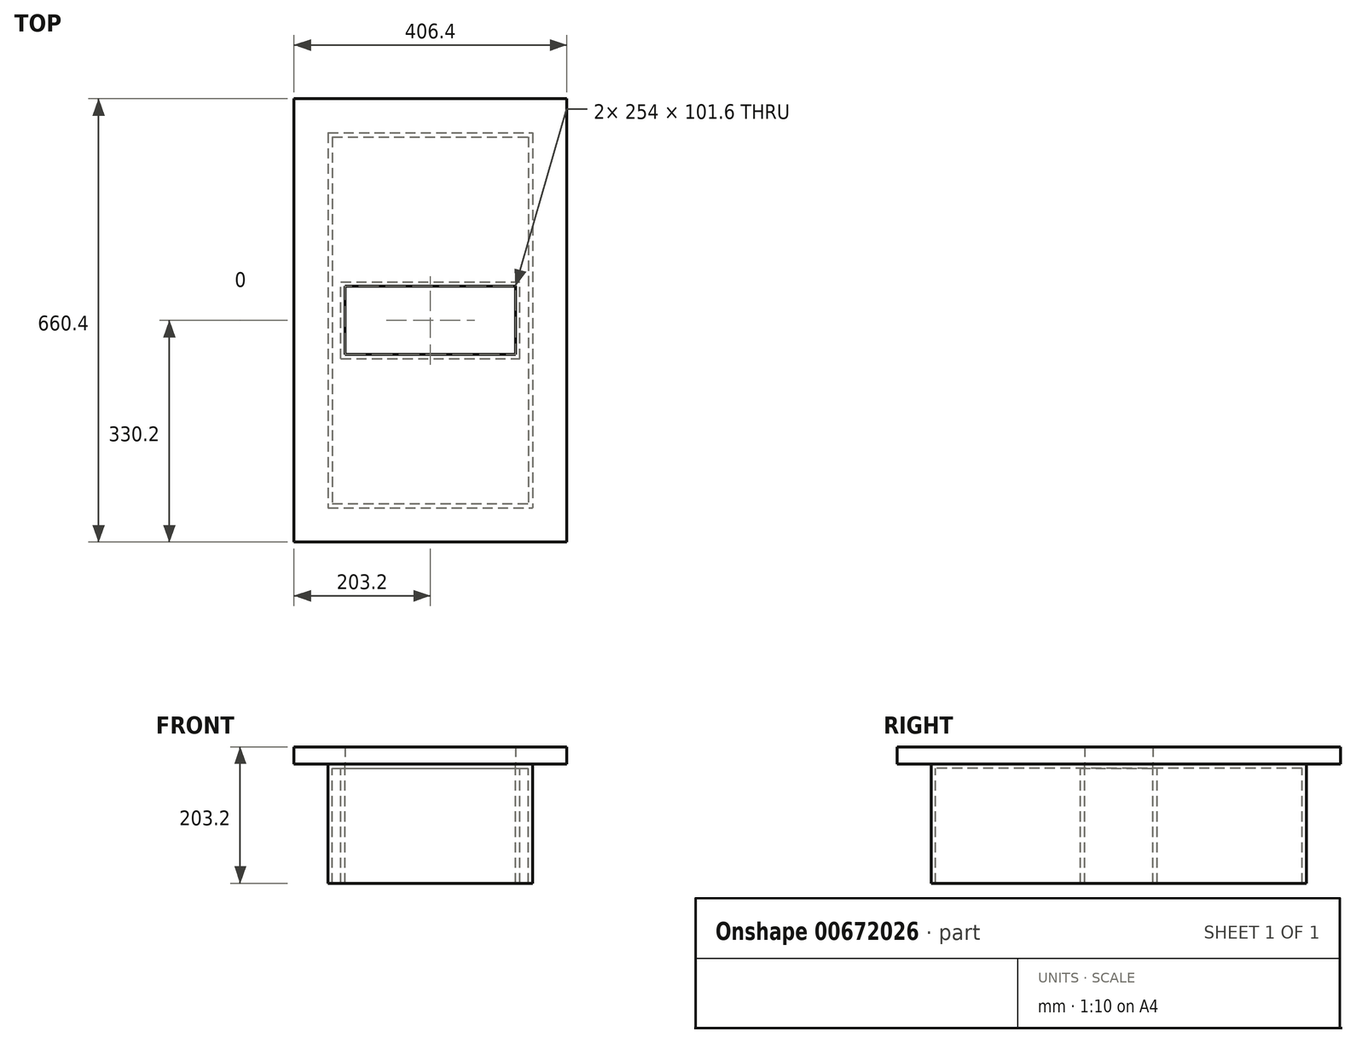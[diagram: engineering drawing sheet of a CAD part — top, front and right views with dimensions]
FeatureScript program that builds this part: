
annotation { "Feature Type Name" : "Feature", "Feature Type Description" : "" }
export const myFeature = defineFeature(function(context is Context, id is Id, definition is map)
    precondition{}
    {
        {
            var Q0;
            Q0=qCreatedBy(makeId("Top.planeOp"),FACE);
            var sketch = newSketch(context, id + "F0", { "sketchPlane" : qUnion([Q0])});
            skLineSegment(sketch, "E0.bottom", {"start": v(152.4, 381) * mm, "end": v(-254, 381) * mm});
            skLineSegment(sketch, "E0.top", {"start": v(152.4, -279.4) * mm, "end": v(-254, -279.4) * mm});
            skLineSegment(sketch, "E0.left", {"start": v(152.4, 381) * mm, "end": v(152.4, -279.4) * mm});
            skLineSegment(sketch, "E0.right", {"start": v(-254, 381) * mm, "end": v(-254, -279.4) * mm});
            skPoint(sketch, "E1", {"position": v(-203.2, 330.2) * mm});
            skPoint(sketch, "E2", {"position": v(101.6, -228.6) * mm});
            skLineSegment(sketch, "E3.bottom", {"start": v(-203.2, 330.2) * mm, "end": v(101.6, 330.2) * mm});
            skLineSegment(sketch, "E3.top", {"start": v(-203.2, -228.6) * mm, "end": v(101.6, -228.6) * mm});
            skLineSegment(sketch, "E3.left", {"start": v(-203.2, 330.2) * mm, "end": v(-203.2, -228.6) * mm});
            skLineSegment(sketch, "E3.right", {"start": v(101.6, 330.2) * mm, "end": v(101.6, -228.6) * mm});
            skLineSegment(sketch, "E4", {"start": v(-177.8, 50.8) * mm, "end": v(76.2, 50.8) * mm, "construction": true});
            skPoint(sketch, "E5", {"position": v(-50.8, 50.8) * mm});
            skPoint(sketch, "E5.positionSnap0", {"position": v(-50.8, 330.2) * mm});
            skLineSegment(sketch, "E6.bottom", {"start": v(-177.8, 0) * mm, "end": v(76.2, 0) * mm});
            skLineSegment(sketch, "E6.top", {"start": v(-177.8, 101.6) * mm, "end": v(76.2, 101.6) * mm});
            skLineSegment(sketch, "E6.left", {"start": v(-177.8, 0) * mm, "end": v(-177.8, 101.6) * mm});
            skLineSegment(sketch, "E6.right", {"start": v(76.2, 0) * mm, "end": v(76.2, 101.6) * mm});
            skSolve(sketch);
        }
        {
            var Q0;
            Q0=makeQuery(id+"F0.imprint","IMPRINT",FACE,{"disambiguationData":[TD([[makeQuery(id+"F0.imprint","IMPRINT",EDGE,{"derivedFrom":sQuery(id+"F0.wireOp",EDGE,"E0.bottom")}),1.0]])]});
            var sketch = newSketch(context, id + "F1", { "sketchPlane" : qUnion([Q0])});
            skSolve(sketch);
        }
        {
            var Q0;
            Q0=makeQuery(id+"F0.imprint","IMPRINT",FACE,{"disambiguationData":[TD([[makeQuery(id+"F0.imprint","IMPRINT",EDGE,{"derivedFrom":sQuery(id+"F0.wireOp",EDGE,"E3.bottom")}),-1.0]])]});
            var Q1;
            Q1=makeQuery(id+"F0.imprint","IMPRINT",FACE,{"disambiguationData":[TD([[makeQuery(id+"F0.imprint","IMPRINT",EDGE,{"derivedFrom":sQuery(id+"F0.wireOp",EDGE,"E0.bottom")}),1.0]])]});
            extrude(context, id + "F2", {"entities" : qUnion([Q0, Q1]), "depth" : 25.4 * mm, "offsetDistance" : 25.4 * mm});
        }
        {
            var Q0;
            Q0=makeQuery(id+"F0.imprint","IMPRINT",FACE,{"disambiguationData":[TD([[makeQuery(id+"F0.imprint","IMPRINT",EDGE,{"derivedFrom":sQuery(id+"F0.wireOp",EDGE,"E3.bottom")}),-1.0]])]});
            extrude(context, id + "F3", {"entities" : qUnion([Q0]), "oppositeDirection" : true, "depth" : 177.8 * mm, "offsetDistance" : 25.4 * mm});
        }
        {
            var Q0;
            Q0=makeQuery(id+"F3.opExtrude","CAP_FACE",FACE,{"disambiguationData":[OSD([sQuery(id+"F0.wireOp",EDGE,"E3.bottom"),sQuery(id+"F0.wireOp",EDGE,"E3.top"),sQuery(id+"F0.wireOp",EDGE,"E3.left"),sQuery(id+"F0.wireOp",EDGE,"E3.right")])],"isStart":false});
            shell(context, id + "F4", {"entities" : qUnion([Q0]), "thickness" : 6.35 * mm});
        }
    });
